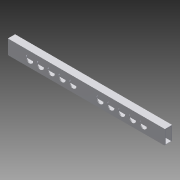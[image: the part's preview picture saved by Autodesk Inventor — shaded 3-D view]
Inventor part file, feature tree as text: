
AUTODESK INVENTOR PART (.ipt)
format: ipt  version: 2015 SP1 (Build 190203100, 203)  size: 156,160 bytes
history: native  units: in
note: dims shown in document units (in); Inventor stores cm internally (conversion verified against a paired STEP export)
features: sketch x3, hole x2, pattern_linear x2, extrude x1, fillet x1
ambient origin geometry x8: Origin, YZ Plane, XZ Plane, XY Plane, X Axis, Y Axis, Z Axis, Center Point
bodies: Solid1 (feature_tree)
feature tree (9):
  extrude  "Extrusion1"  Depth=1.0in
  fillet  "Fillet1"  Radius=1.75in
  hole  "Hole3"  [1 undecoded]
  pattern_linear  "Rectangular Pattern3"  Spacing1=21.75in  [1 undecoded]
  hole  "Hole4"  [1 undecoded]
  pattern_linear  "Rectangular Pattern4"  Spacing1=1.0in  [1 undecoded]
  sketch  "Sketch1"  dims[d0=2.0in d1=1.0in d2=1.75in]
  sketch  "Sketch4"  dims[d3=0.75in d4=0.125in]
  sketch  "Sketch5"  dims[d5=0.125in d6=21.75in d7=0.0in d32=0.125in d33=1.0in d34=3.0in d35=1.0in d36=0.75in d37=0.375in d38=0.25in d39=0.5635in d40=1.0in d41=0.8108in d42=1.9685in d44=1.5in d45=3.0in d46=1.0in d47=1.0in d48=0.75in d49=0.375in d50=0.25in d51=0.5635in d52=1.0in d53=0.8108in d54=1.9685in d56=1.5in]
note: 4 required parameter values undecoded (feature->parameter linkage not recoverable at this tier; creation-order binding heuristic only, values carry confidence <= 0.55)
